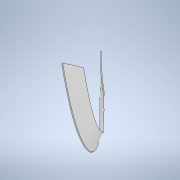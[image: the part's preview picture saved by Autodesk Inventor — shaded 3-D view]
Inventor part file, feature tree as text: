
AUTODESK INVENTOR PART (.ipt)
format: ipt  version: 2021 (Build 250183000, 183)  size: 161,792 bytes
history: native  units: in
note: dims shown in document units (in); Inventor stores cm internally (conversion verified against a paired STEP export)
features: sketch x2, sweep x1
ambient origin geometry x8: Origin, YZ Plane, XZ Plane, XY Plane, X Axis, Y Axis, Z Axis, Center Point
bodies: Body1 (feature_tree)
feature tree (3):
  sweep  "Sweep2"
  sketch  "3D Sketch1"
  sketch  "Sketch2"  dims[d12=2.0in d13=0.1in d14=0.0in d15=0.0in]
